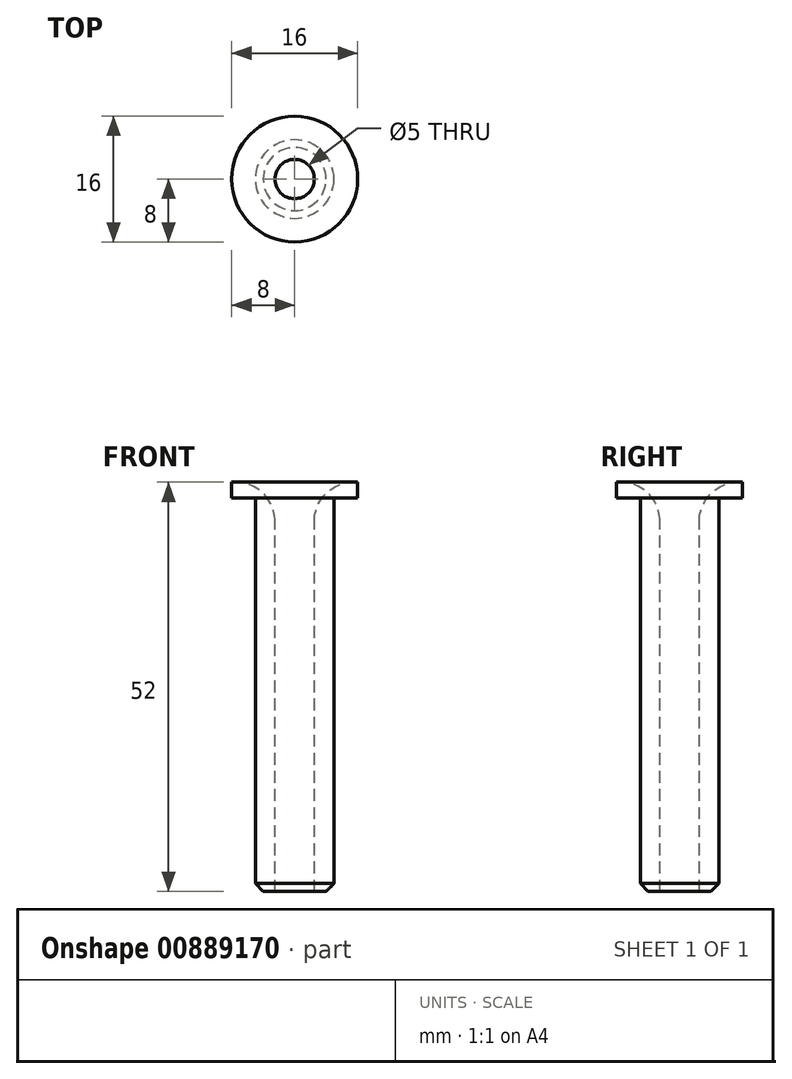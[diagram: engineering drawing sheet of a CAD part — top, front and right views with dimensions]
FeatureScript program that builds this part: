
annotation { "Feature Type Name" : "Feature", "Feature Type Description" : "" }
export const myFeature = defineFeature(function(context is Context, id is Id, definition is map)
    precondition{}
    {
        {
            var Q0;
            Q0=qCreatedBy(makeId("Front.planeOp"),FACE);
            var sketch = newSketch(context, id + "F0", { "sketchPlane" : qUnion([Q0])});
            skLineSegment(sketch, "E0", {"start": v(0, 51.06) * mm, "end": v(0, -5.43) * mm, "construction": true});
            skLineSegment(sketch, "E1", {"start": v(2.5, 0) * mm, "end": v(2.5, 52) * mm});
            skLineSegment(sketch, "E2", {"start": v(2.5, 0) * mm, "end": v(5, 0) * mm});
            skLineSegment(sketch, "E3", {"start": v(5, 0) * mm, "end": v(5, 50) * mm});
            skLineSegment(sketch, "E4", {"start": v(5, 50) * mm, "end": v(8, 50) * mm});
            skLineSegment(sketch, "E5", {"start": v(8, 50) * mm, "end": v(8, 52) * mm});
            skLineSegment(sketch, "E6", {"start": v(8, 52) * mm, "end": v(2.5, 52) * mm});
            skLineSegment(sketch, "E7", {"start": v(0, 0) * mm, "end": v(-0.3, 0) * mm, "construction": true});
            skSolve(sketch);
        }
        {
            var Q0;
            Q0=makeQuery(id+"F0.imprint","IMPRINT",FACE,{"disambiguationData":[TD([[makeQuery(id+"F0.imprint","IMPRINT",EDGE,{"derivedFrom":sQuery(id+"F0.wireOp",EDGE,"E1")}),-1.0]])]});
            var Q1;
            Q1=sQuery(id+"F0.wireOp",EDGE,"E0");
            revolve(context, id + "F1", {"surfaceOperationType" : NewSurfaceOperationType.NEW, "entities" : qUnion([Q0]), "axis" : qUnion([Q1]), "revolveType" : RevolveType.FULL});
        }
        {
            var Q0;
            Q0=makeQuery(id+"F1.opRevolve","SWEPT_EDGE",EDGE,{"disambiguationData":[OSD([sQuery(id+"F0.wireOp",EDGE,"E1"),sQuery(id+"F0.wireOp",EDGE,"E6")])]});
            fillet(context, id + "F2", {"entities" : qUnion([Q0]), "radius" : 5 * mm, "tangentPropagation" : true, "allowEdgeOverflow" : false});
        }
        {
            var Q0;
            Q0=makeQuery(id+"F1.opRevolve","SWEPT_EDGE",EDGE,{"disambiguationData":[OSD([sQuery(id+"F0.wireOp",EDGE,"E2"),sQuery(id+"F0.wireOp",EDGE,"E3")])]});
            chamfer(context, id + "F3", {"entities" : qUnion([Q0]), "width" : 1 * mm, "tangentPropagation" : true});
        }
    });
